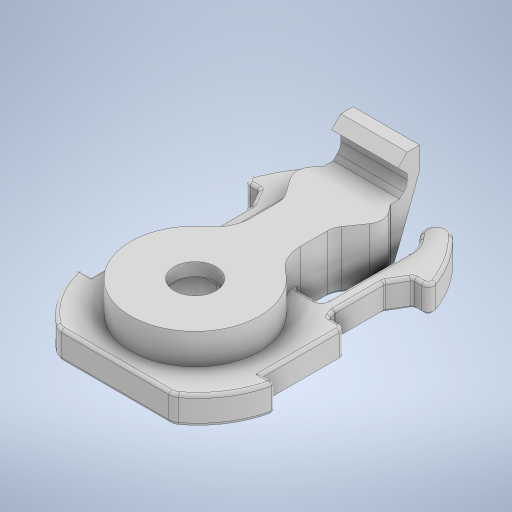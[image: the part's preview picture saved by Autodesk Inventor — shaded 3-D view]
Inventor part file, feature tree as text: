
AUTODESK INVENTOR PART (.ipt)
format: ipt  version: 2024 (Build 280153000, 153)  size: 813,568 bytes
history: native  units: in
note: dims shown in document units (in); Inventor stores cm internally (conversion verified against a paired STEP export)
features: extrude x8, chamfer x5, direct_edit x4, fillet x4, move_body x4, sketch x3, revolve x1
ambient origin geometry x8: Origin, YZ Plane, XZ Plane, XY Plane, X Axis, Y Axis, Z Axis, Center Point
bodies: Solid1 (feature_tree)
feature tree (29):
  sketch  "Sketch1"  dims[d0=0.5348in d1=0.0394in]
  extrude  "Extrusion1"  Depth=0.0394in
  extrude  "Extrusion2"  Depth=0.0197in
  sketch  "Sketch2"  dims[d2=0.0197in d3=0.0197in]
  extrude  "Extrusion3"  Depth=0.6201in
  extrude  "Extrusion4"  Depth=0.0118in
  extrude  "Extrusion5"  Depth=0.0118in
  extrude  "Extrusion6"  Depth=0.0118in
  direct_edit  "Direct Edit1"
  extrude  "Extrusion7"  Depth=0.0118in
  chamfer  "Chamfer1"  Distance=0.0787in
  direct_edit  "Direct Edit2"
  extrude  "Extrusion8"  Depth=0.0118in
  chamfer  "Chamfer2"  Distance=0.1476in
  chamfer  "Chamfer3"  Distance=0.315in
  fillet  "Fillet1"  Radius=0.126in
  direct_edit  "Direct Edit3"
  direct_edit  "Direct Edit4"
  fillet  "Fillet2"  Radius=0.1843in
  fillet  "Fillet4"  Radius=0.0831in
  fillet  "Fillet5"  Radius=0.0394in
  chamfer  "Chamfer4"  Distance=0.013in
  chamfer  "Chamfer5"  Distance=0.089in
  sketch  "Sketch3"  dims[d4=0.0197in d5=0.6201in d6=0.4882in d7=1.1063in d8=1.028in d9=0.122in d10=0.0787in d11=0.0118in d12=0.1476in d13=0.315in d14=0.126in d15=0.1843in d16=0.0831in d17=0.0394in d18=0.013in d19=0.089in d20=0.0783in d21=0.1252in d23=0.1752in d24=0.962in d26=45.0deg d27=0.8465in d28=0.0661in d29=0.2031in d30=0.3016in d31=0.052in d32=0.0394in d34=0.9963in d35=0.2213in d36=0.2542in d37=0.0591in d38=0.1083in d39=0.5898in d40=0.0059in d41=0.1575in d42=0.0394in d43=0.1575in d44=0.0in d45=1.4724in d46=0.087in d47=0.0984in d48=0.0in d49=0.4862in d50=0.2677in d51=0.0in d52=0.7087in d53=0.2165in d54=0.0in d55=0.1181in d56=0.1575in d57=0.0in d58=0.0in d59=0.126in d60=0.0in d61=0.1339in d62=0.0in d63=0.1575in d64=0.0in d65=0.0in d66=0.0197in d67=1.2254in d68=0.0787in d69=0.4252in d70=0.4528in d71=0.0in d72=0.1575in d73=0.0787in d74=45.0deg d75=0.0in d76=0.0in d77=-0.1875in d78=0.1181in d79=0.0591in d80=0.0in d81=0.0591in d82=0.0787in d83=45.0deg d84=0.0492in d85=0.0787in d86=45.0deg d87=0.0787in d88=0.1718in d89=0.0in d90=0.0in d91=-0.0551in d92=0.0in d93=0.0in d94=-0.0551in d95=0.2362in d97=0.0197in d98=0.0197in d99=0.0197in d100=0.0787in d101=45.0deg d102=0.0118in d103=0.0197in d104=45.0deg]
  move_body  "Move1"
  move_body  "Move2"
  revolve  "Rotate1"  [1 undecoded]
  move_body  "Move3"
  move_body  "Move4"
note: 1 required parameter value undecoded (feature->parameter linkage not recoverable at this tier; creation-order binding heuristic only, values carry confidence <= 0.55)
